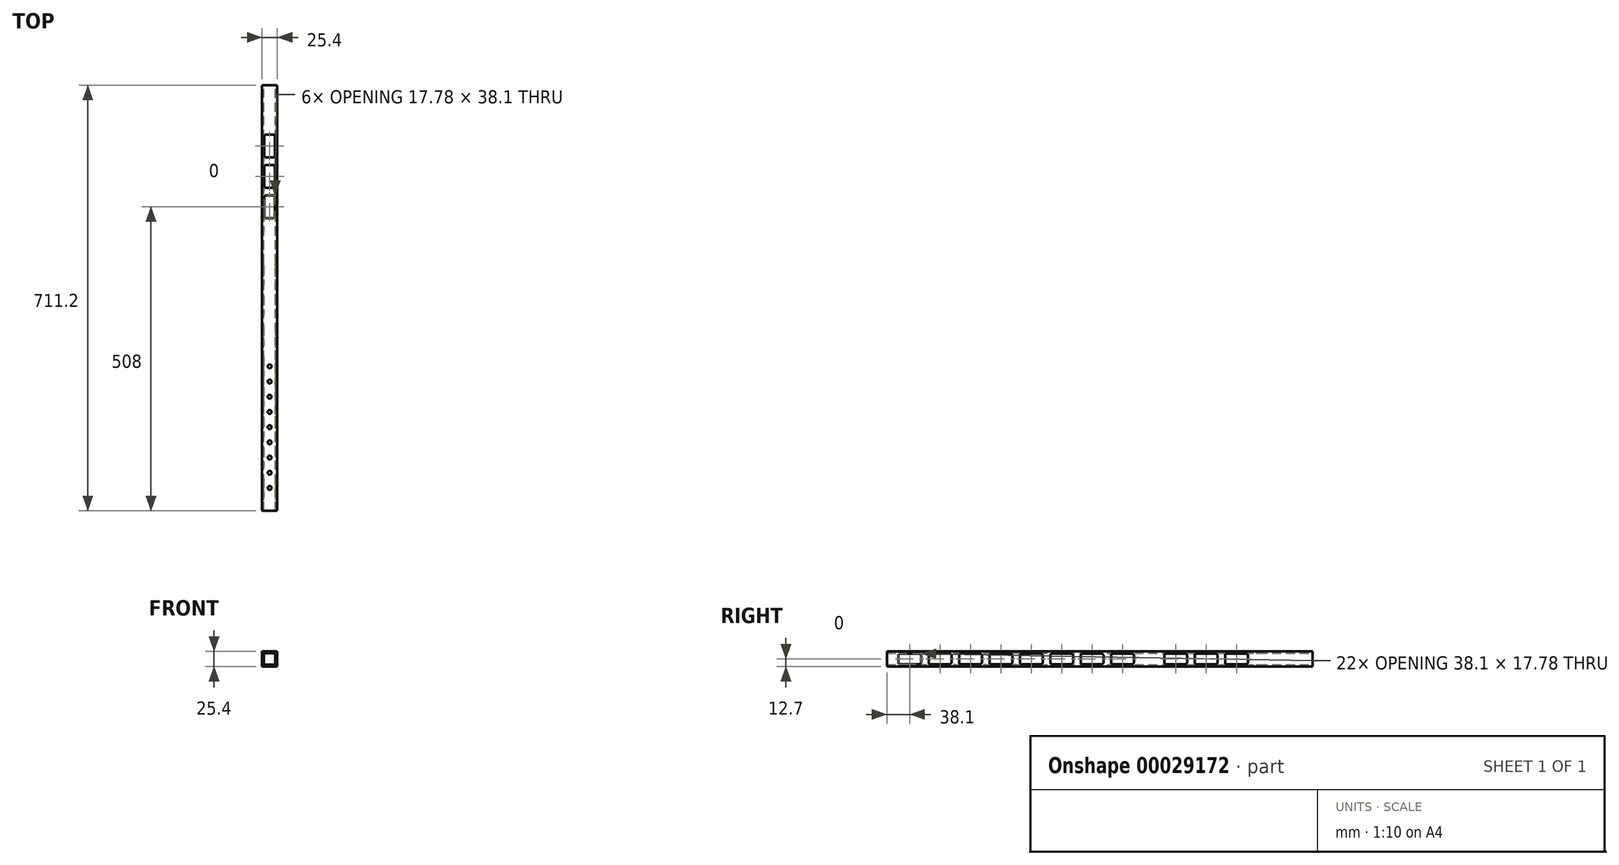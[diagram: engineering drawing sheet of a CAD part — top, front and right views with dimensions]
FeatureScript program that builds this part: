
annotation { "Feature Type Name" : "Feature", "Feature Type Description" : "" }
export const myFeature = defineFeature(function(context is Context, id is Id, definition is map)
    precondition{}
    {
        {
            var Q0;
            Q0=qCreatedBy(makeId("Front.planeOp"),FACE);
            var sketch = newSketch(context, id + "F0", { "sketchPlane" : qUnion([Q0])});
            skLineSegment(sketch, "E0.rect.bottom", {"start": v(12.7, 12.7) * mm, "end": v(-12.7, 12.7) * mm});
            skLineSegment(sketch, "E0.rect.top", {"start": v(12.7, -12.7) * mm, "end": v(-12.7, -12.7) * mm});
            skLineSegment(sketch, "E0.rect.left", {"start": v(12.7, 12.7) * mm, "end": v(12.7, -12.7) * mm});
            skLineSegment(sketch, "E0.rect.right", {"start": v(-12.7, 12.7) * mm, "end": v(-12.7, -12.7) * mm});
            skPoint(sketch, "E0.rect.middle", {"position": v(0, 0) * mm});
            skLineSegment(sketch, "E1.rect.bottom", {"start": v(9.53, 9.53) * mm, "end": v(-9.53, 9.53) * mm});
            skLineSegment(sketch, "E1.rect.top", {"start": v(9.53, -9.53) * mm, "end": v(-9.53, -9.53) * mm});
            skLineSegment(sketch, "E1.rect.left", {"start": v(9.53, 9.53) * mm, "end": v(9.53, -9.53) * mm});
            skLineSegment(sketch, "E1.rect.right", {"start": v(-9.53, 9.53) * mm, "end": v(-9.53, -9.53) * mm});
            skSolve(sketch);
        }
        {
            var Q0;
            Q0=makeQuery(id+"F0.imprint","IMPRINT",FACE,{"disambiguationData":[TD([[makeQuery(id+"F0.imprint","IMPRINT",EDGE,{"derivedFrom":sQuery(id+"F0.wireOp",EDGE,"E0.rect.bottom")}),1.0]])]});
            extrude(context, id + "F1", {"entities" : qUnion([Q0]), "depth" : 279.4 * mm});
        }
        {
            var Q0;
            Q0=makeQuery(id+"F1.opExtrude","CAP_FACE",FACE,{"disambiguationData":[OSD([sQuery(id+"F0.wireOp",EDGE,"E0.rect.bottom"),sQuery(id+"F0.wireOp",EDGE,"E0.rect.top"),sQuery(id+"F0.wireOp",EDGE,"E0.rect.left"),sQuery(id+"F0.wireOp",EDGE,"E0.rect.right"),sQuery(id+"F0.wireOp",EDGE,"E1.rect.bottom"),sQuery(id+"F0.wireOp",EDGE,"E1.rect.top"),sQuery(id+"F0.wireOp",EDGE,"E1.rect.left"),sQuery(id+"F0.wireOp",EDGE,"E1.rect.right")])],"isStart":false});
            extrude(context, id + "F2", {"entities" : qUnion([Q0]), "operationType" : NewBodyOperationType.ADD, "depth" : 431.8 * mm});
        }
        {
            var Q0;
            {var subQ0=sQuery(id+"F0.wireOp",EDGE,"E0.rect.bottom");Q0=makeQuery(id+"F2.boolean.opBoolean","MERGE",FACE,{"derivedFrom":[makeQuery(id+"F1.opExtrude","SWEPT_FACE",FACE,{"disambiguationData":[OSD([subQ0])]}),makeQuery(id+"F2.opExtrude","SWEPT_FACE",FACE,{"disambiguationData":[OSD([subQ0])]})]});}
            var sketch = newSketch(context, id + "F3", { "sketchPlane" : qUnion([Q0])});
            skLineSegment(sketch, "E2", {"start": v(0, -711.2) * mm, "end": v(0, -676.27) * mm});
            skCircle(sketch, "E3", {"center": v(0, -469.9) * mm, "radius": 3.18 * mm});
            skLineSegment(sketch, "E4.trimOffspring", {"start": v(0, -466.73) * mm, "end": v(0, -120.65) * mm});
            skCircle(sketch, "E5", {"center": v(0, -495.3) * mm, "radius": 3.18 * mm});
            skLineSegment(sketch, "E6.trimOffspring", {"start": v(0, -492.13) * mm, "end": v(0, -473.08) * mm});
            skCircle(sketch, "E7", {"center": v(0, -520.7) * mm, "radius": 3.18 * mm});
            skLineSegment(sketch, "E8.trimOffspring", {"start": v(0, -517.52) * mm, "end": v(0, -498.48) * mm});
            skCircle(sketch, "E9", {"center": v(0, -546.1) * mm, "radius": 3.18 * mm});
            skCircle(sketch, "E10", {"center": v(0, -571.5) * mm, "radius": 3.18 * mm});
            skLineSegment(sketch, "E11.trimOffspring", {"start": v(0, -542.92) * mm, "end": v(0, -523.88) * mm});
            skLineSegment(sketch, "E12", {"start": v(0, -549.28) * mm, "end": v(0, -568.32) * mm});
            skCircle(sketch, "E13", {"center": v(0, -596.9) * mm, "radius": 3.18 * mm});
            skLineSegment(sketch, "E14.trimOffspring", {"start": v(0, -593.72) * mm, "end": v(0, -574.68) * mm});
            skCircle(sketch, "E15", {"center": v(0, -622.3) * mm, "radius": 3.18 * mm});
            skLineSegment(sketch, "E16.trimOffspring", {"start": v(0, -619.12) * mm, "end": v(0, -600.08) * mm});
            skCircle(sketch, "E17", {"center": v(0, -647.7) * mm, "radius": 3.18 * mm});
            skLineSegment(sketch, "E18.trimOffspring", {"start": v(0, -644.52) * mm, "end": v(0, -625.48) * mm});
            skCircle(sketch, "E19", {"center": v(0, -673.1) * mm, "radius": 3.18 * mm});
            skLineSegment(sketch, "E20.trimOffspring", {"start": v(0, -669.92) * mm, "end": v(0, -650.88) * mm});
            skLineSegment(sketch, "E21.rect.bottom", {"start": v(-5.71, -82.55) * mm, "end": v(5.72, -82.55) * mm});
            skLineSegment(sketch, "E21.rect.top", {"start": v(-5.71, -120.65) * mm, "end": v(5.72, -120.65) * mm});
            skLineSegment(sketch, "E21.rect.left", {"start": v(-8.89, -85.73) * mm, "end": v(-8.89, -117.48) * mm});
            skLineSegment(sketch, "E21.rect.right", {"start": v(8.9, -85.73) * mm, "end": v(8.9, -117.48) * mm});
            skPoint(sketch, "E21.rect.middle", {"position": v(0, -101.6) * mm});
            skPoint(sketch, "E22.visualSharp", {"position": v(-8.89, -82.55) * mm});
            skArc(sketch, "E22.filletArc", {"start": v(-5.71, -82.55) * mm, "mid": v(-7.96, -83.48) * mm, "end": v(-8.89, -85.73) * mm});
            skPoint(sketch, "E23.visualSharp", {"position": v(8.9, -82.55) * mm});
            skArc(sketch, "E23.filletArc", {"start": v(8.9, -85.73) * mm, "mid": v(7.96, -83.48) * mm, "end": v(5.72, -82.55) * mm});
            skPoint(sketch, "E24.visualSharp", {"position": v(-8.89, -120.65) * mm});
            skArc(sketch, "E24.filletArc", {"start": v(-8.89, -117.48) * mm, "mid": v(-7.96, -119.72) * mm, "end": v(-5.71, -120.65) * mm});
            skPoint(sketch, "E25.visualSharp", {"position": v(8.9, -120.65) * mm});
            skArc(sketch, "E25.filletArc", {"start": v(5.72, -120.65) * mm, "mid": v(7.96, -119.72) * mm, "end": v(8.9, -117.48) * mm});
            skPoint(sketch, "E26", {"position": v(0, -82.55) * mm});
            skLineSegment(sketch, "E27.trimOffspring", {"start": v(0, -82.55) * mm, "end": v(0, 0) * mm});
            skLineSegment(sketch, "E28.0.1.0", {"start": v(-5.71, -171.45) * mm, "end": v(5.72, -171.45) * mm});
            skArc(sketch, "E28.0.1.1", {"start": v(5.72, -171.45) * mm, "mid": v(7.96, -170.52) * mm, "end": v(8.9, -168.28) * mm});
            skLineSegment(sketch, "E28.0.1.2", {"start": v(8.9, -136.53) * mm, "end": v(8.9, -168.28) * mm});
            skArc(sketch, "E28.0.1.3", {"start": v(8.9, -136.53) * mm, "mid": v(7.96, -134.28) * mm, "end": v(5.72, -133.35) * mm});
            skLineSegment(sketch, "E28.0.1.4", {"start": v(-5.71, -133.35) * mm, "end": v(5.72, -133.35) * mm});
            skArc(sketch, "E28.0.1.5", {"start": v(-5.71, -133.35) * mm, "mid": v(-7.96, -134.28) * mm, "end": v(-8.89, -136.53) * mm});
            skLineSegment(sketch, "E28.0.1.6", {"start": v(-8.89, -136.53) * mm, "end": v(-8.89, -168.28) * mm});
            skArc(sketch, "E28.0.1.7", {"start": v(-8.89, -168.28) * mm, "mid": v(-7.96, -170.52) * mm, "end": v(-5.71, -171.45) * mm});
            skLineSegment(sketch, "E28.0.2.0", {"start": v(-5.71, -222.25) * mm, "end": v(5.72, -222.25) * mm});
            skArc(sketch, "E28.0.2.1", {"start": v(5.72, -222.25) * mm, "mid": v(7.96, -221.32) * mm, "end": v(8.9, -219.08) * mm});
            skLineSegment(sketch, "E28.0.2.2", {"start": v(8.9, -187.33) * mm, "end": v(8.9, -219.08) * mm});
            skArc(sketch, "E28.0.2.3", {"start": v(8.9, -187.33) * mm, "mid": v(7.96, -185.08) * mm, "end": v(5.72, -184.15) * mm});
            skLineSegment(sketch, "E28.0.2.4", {"start": v(-5.71, -184.15) * mm, "end": v(5.72, -184.15) * mm});
            skArc(sketch, "E28.0.2.5", {"start": v(-5.71, -184.15) * mm, "mid": v(-7.96, -185.08) * mm, "end": v(-8.89, -187.33) * mm});
            skLineSegment(sketch, "E28.0.2.6", {"start": v(-8.89, -187.33) * mm, "end": v(-8.89, -219.08) * mm});
            skArc(sketch, "E28.0.2.7", {"start": v(-8.89, -219.08) * mm, "mid": v(-7.96, -221.32) * mm, "end": v(-5.71, -222.25) * mm});
            skLineSegment(sketch, "E28.direction1", {"start": v(-5.71, -120.65) * mm, "end": v(44.46, -120.65) * mm, "construction": true});
            skLineSegment(sketch, "E28.direction2", {"start": v(-5.71, -120.65) * mm, "end": v(-5.71, -171.45) * mm, "construction": true});
            skSolve(sketch);
        }
        {
            var Q0;
            {var subQ0=sQuery(id+"F3.wireOp",EDGE,"E3");var subQ2=makeQuery(id+"F3.imprint","INTERSECT",VERTEX,{"derivedFrom":[sQuery(id+"F3.wireOp",EDGE,"E2"),subQ0]});Q0=makeQuery(id+"F3.imprint","IMPRINT",FACE,{"disambiguationData":[TD([[makeQuery(id+"F3.imprint","IMPRINT",EDGE,{"disambiguationData":[TD([[subQ2,1.0]])],"derivedFrom":subQ0}),1.0]])]});}
            extrude(context, id + "F4", {"entities" : qUnion([Q0]), "operationType" : NewBodyOperationType.REMOVE, "oppositeDirection" : true, "depth" : 25.4 * mm});
        }
        {
            var Q0;
            Q0 = qSketchRegion(id + "F3", true);
            extrude(context, id + "F5", {"entities" : qUnion([Q0]), "operationType" : NewBodyOperationType.REMOVE, "oppositeDirection" : true, "depth" : 25.4 * mm});
        }
        {
            var Q0;
            {var subQ0=sQuery(id+"F0.wireOp",EDGE,"E0.rect.left");Q0=makeQuery(id+"F2.boolean.opBoolean","MERGE",FACE,{"derivedFrom":[makeQuery(id+"F1.opExtrude","SWEPT_FACE",FACE,{"disambiguationData":[OSD([subQ0])]}),makeQuery(id+"F2.opExtrude","SWEPT_FACE",FACE,{"disambiguationData":[OSD([subQ0])]})]});}
            var sketch = newSketch(context, id + "F6", { "sketchPlane" : qUnion([Q0])});
            skLineSegment(sketch, "E29", {"start": v(0, 0) * mm, "end": v(-57.15, 0) * mm});
            skLineSegment(sketch, "E30.rect.bottom", {"start": v(-657.23, -8.9) * mm, "end": v(-688.98, -8.9) * mm});
            skLineSegment(sketch, "E30.rect.top", {"start": v(-657.23, 8.9) * mm, "end": v(-688.98, 8.9) * mm});
            skLineSegment(sketch, "E30.rect.left", {"start": v(-654.05, -5.72) * mm, "end": v(-654.05, 5.72) * mm});
            skLineSegment(sketch, "E30.rect.right", {"start": v(-692.15, -5.72) * mm, "end": v(-692.15, 5.72) * mm});
            skPoint(sketch, "E30.rect.middle", {"position": v(-673.1, 0) * mm});
            skPoint(sketch, "E31.visualSharp", {"position": v(-654.05, 8.89) * mm});
            skArc(sketch, "E31.filletArc", {"start": v(-654.05, 5.72) * mm, "mid": v(-654.98, 7.96) * mm, "end": v(-657.23, 8.9) * mm});
            skPoint(sketch, "E32.visualSharp", {"position": v(-654.05, -8.9) * mm});
            skArc(sketch, "E32.filletArc", {"start": v(-657.23, -8.9) * mm, "mid": v(-654.98, -7.96) * mm, "end": v(-654.05, -5.72) * mm});
            skPoint(sketch, "E33.visualSharp", {"position": v(-692.15, -8.9) * mm});
            skArc(sketch, "E33.filletArc", {"start": v(-692.15, -5.72) * mm, "mid": v(-691.22, -7.96) * mm, "end": v(-688.98, -8.9) * mm});
            skPoint(sketch, "E34.visualSharp", {"position": v(-692.15, 8.89) * mm});
            skArc(sketch, "E34.filletArc", {"start": v(-688.98, 8.9) * mm, "mid": v(-691.22, 7.96) * mm, "end": v(-692.15, 5.72) * mm});
            skLineSegment(sketch, "E35.trimOffspring", {"start": v(-692.15, 0) * mm, "end": v(-711.2, 0) * mm});
            skLineSegment(sketch, "E36.1.0.0", {"start": v(-603.25, -5.72) * mm, "end": v(-603.25, 5.72) * mm});
            skArc(sketch, "E36.1.0.1", {"start": v(-603.25, 5.72) * mm, "mid": v(-604.18, 7.96) * mm, "end": v(-606.43, 8.9) * mm});
            skLineSegment(sketch, "E36.1.0.2", {"start": v(-606.43, -8.9) * mm, "end": v(-638.18, -8.9) * mm});
            skArc(sketch, "E36.1.0.3", {"start": v(-606.43, -8.9) * mm, "mid": v(-604.18, -7.96) * mm, "end": v(-603.25, -5.72) * mm});
            skLineSegment(sketch, "E36.1.0.4", {"start": v(-606.43, 8.9) * mm, "end": v(-638.18, 8.9) * mm});
            skArc(sketch, "E36.1.0.5", {"start": v(-638.18, 8.9) * mm, "mid": v(-640.42, 7.96) * mm, "end": v(-641.35, 5.72) * mm});
            skLineSegment(sketch, "E36.1.0.6", {"start": v(-641.35, -5.72) * mm, "end": v(-641.35, 5.72) * mm});
            skArc(sketch, "E36.1.0.7", {"start": v(-641.35, -5.72) * mm, "mid": v(-640.42, -7.96) * mm, "end": v(-638.18, -8.9) * mm});
            skLineSegment(sketch, "E36.2.0.0", {"start": v(-552.45, -5.72) * mm, "end": v(-552.45, 5.72) * mm});
            skArc(sketch, "E36.2.0.1", {"start": v(-552.45, 5.72) * mm, "mid": v(-553.38, 7.96) * mm, "end": v(-555.63, 8.9) * mm});
            skLineSegment(sketch, "E36.2.0.2", {"start": v(-555.63, -8.9) * mm, "end": v(-587.38, -8.9) * mm});
            skArc(sketch, "E36.2.0.3", {"start": v(-555.63, -8.9) * mm, "mid": v(-553.38, -7.96) * mm, "end": v(-552.45, -5.72) * mm});
            skLineSegment(sketch, "E36.2.0.4", {"start": v(-555.63, 8.9) * mm, "end": v(-587.38, 8.9) * mm});
            skArc(sketch, "E36.2.0.5", {"start": v(-587.38, 8.9) * mm, "mid": v(-589.62, 7.96) * mm, "end": v(-590.55, 5.72) * mm});
            skLineSegment(sketch, "E36.2.0.6", {"start": v(-590.55, -5.72) * mm, "end": v(-590.55, 5.72) * mm});
            skArc(sketch, "E36.2.0.7", {"start": v(-590.55, -5.72) * mm, "mid": v(-589.62, -7.96) * mm, "end": v(-587.38, -8.9) * mm});
            skLineSegment(sketch, "E36.3.0.0", {"start": v(-501.65, -5.72) * mm, "end": v(-501.65, 5.72) * mm});
            skArc(sketch, "E36.3.0.1", {"start": v(-501.65, 5.72) * mm, "mid": v(-502.58, 7.96) * mm, "end": v(-504.83, 8.9) * mm});
            skLineSegment(sketch, "E36.3.0.2", {"start": v(-504.83, -8.9) * mm, "end": v(-536.58, -8.9) * mm});
            skArc(sketch, "E36.3.0.3", {"start": v(-504.83, -8.9) * mm, "mid": v(-502.58, -7.96) * mm, "end": v(-501.65, -5.72) * mm});
            skLineSegment(sketch, "E36.3.0.4", {"start": v(-504.83, 8.9) * mm, "end": v(-536.58, 8.9) * mm});
            skArc(sketch, "E36.3.0.5", {"start": v(-536.58, 8.9) * mm, "mid": v(-538.82, 7.96) * mm, "end": v(-539.75, 5.72) * mm});
            skLineSegment(sketch, "E36.3.0.6", {"start": v(-539.75, -5.72) * mm, "end": v(-539.75, 5.72) * mm});
            skArc(sketch, "E36.3.0.7", {"start": v(-539.75, -5.72) * mm, "mid": v(-538.82, -7.96) * mm, "end": v(-536.58, -8.9) * mm});
            skLineSegment(sketch, "E36.4.0.0", {"start": v(-450.85, -5.72) * mm, "end": v(-450.85, 5.72) * mm});
            skArc(sketch, "E36.4.0.1", {"start": v(-450.85, 5.72) * mm, "mid": v(-451.78, 7.96) * mm, "end": v(-454.03, 8.9) * mm});
            skLineSegment(sketch, "E36.4.0.2", {"start": v(-454.03, -8.9) * mm, "end": v(-485.78, -8.9) * mm});
            skArc(sketch, "E36.4.0.3", {"start": v(-454.03, -8.9) * mm, "mid": v(-451.78, -7.96) * mm, "end": v(-450.85, -5.72) * mm});
            skLineSegment(sketch, "E36.4.0.4", {"start": v(-454.03, 8.9) * mm, "end": v(-485.78, 8.9) * mm});
            skArc(sketch, "E36.4.0.5", {"start": v(-485.78, 8.9) * mm, "mid": v(-488.02, 7.96) * mm, "end": v(-488.95, 5.72) * mm});
            skLineSegment(sketch, "E36.4.0.6", {"start": v(-488.95, -5.72) * mm, "end": v(-488.95, 5.72) * mm});
            skArc(sketch, "E36.4.0.7", {"start": v(-488.95, -5.72) * mm, "mid": v(-488.02, -7.96) * mm, "end": v(-485.78, -8.9) * mm});
            skLineSegment(sketch, "E36.5.0.0", {"start": v(-400.05, -5.72) * mm, "end": v(-400.05, 5.72) * mm});
            skArc(sketch, "E36.5.0.1", {"start": v(-400.05, 5.72) * mm, "mid": v(-400.98, 7.96) * mm, "end": v(-403.23, 8.9) * mm});
            skLineSegment(sketch, "E36.5.0.2", {"start": v(-403.23, -8.9) * mm, "end": v(-434.98, -8.9) * mm});
            skArc(sketch, "E36.5.0.3", {"start": v(-403.23, -8.9) * mm, "mid": v(-400.98, -7.96) * mm, "end": v(-400.05, -5.72) * mm});
            skLineSegment(sketch, "E36.5.0.4", {"start": v(-403.23, 8.9) * mm, "end": v(-434.98, 8.9) * mm});
            skArc(sketch, "E36.5.0.5", {"start": v(-434.98, 8.9) * mm, "mid": v(-437.22, 7.96) * mm, "end": v(-438.15, 5.72) * mm});
            skLineSegment(sketch, "E36.5.0.6", {"start": v(-438.15, -5.72) * mm, "end": v(-438.15, 5.72) * mm});
            skArc(sketch, "E36.5.0.7", {"start": v(-438.15, -5.72) * mm, "mid": v(-437.22, -7.96) * mm, "end": v(-434.98, -8.9) * mm});
            skLineSegment(sketch, "E36.6.0.0", {"start": v(-349.25, -5.72) * mm, "end": v(-349.25, 5.72) * mm});
            skArc(sketch, "E36.6.0.1", {"start": v(-349.25, 5.72) * mm, "mid": v(-350.18, 7.96) * mm, "end": v(-352.43, 8.9) * mm});
            skLineSegment(sketch, "E36.6.0.2", {"start": v(-352.43, -8.9) * mm, "end": v(-384.18, -8.9) * mm});
            skArc(sketch, "E36.6.0.3", {"start": v(-352.43, -8.9) * mm, "mid": v(-350.18, -7.96) * mm, "end": v(-349.25, -5.72) * mm});
            skLineSegment(sketch, "E36.6.0.4", {"start": v(-352.43, 8.9) * mm, "end": v(-384.18, 8.9) * mm});
            skArc(sketch, "E36.6.0.5", {"start": v(-384.18, 8.9) * mm, "mid": v(-386.42, 7.96) * mm, "end": v(-387.35, 5.72) * mm});
            skLineSegment(sketch, "E36.6.0.6", {"start": v(-387.35, -5.72) * mm, "end": v(-387.35, 5.72) * mm});
            skArc(sketch, "E36.6.0.7", {"start": v(-387.35, -5.72) * mm, "mid": v(-386.42, -7.96) * mm, "end": v(-384.18, -8.9) * mm});
            skLineSegment(sketch, "E36.7.0.0", {"start": v(-298.45, -5.72) * mm, "end": v(-298.45, 5.72) * mm});
            skArc(sketch, "E36.7.0.1", {"start": v(-298.45, 5.72) * mm, "mid": v(-299.38, 7.96) * mm, "end": v(-301.63, 8.9) * mm});
            skLineSegment(sketch, "E36.7.0.2", {"start": v(-301.63, -8.9) * mm, "end": v(-333.38, -8.9) * mm});
            skArc(sketch, "E36.7.0.3", {"start": v(-301.63, -8.9) * mm, "mid": v(-299.38, -7.96) * mm, "end": v(-298.45, -5.72) * mm});
            skLineSegment(sketch, "E36.7.0.4", {"start": v(-301.63, 8.9) * mm, "end": v(-333.38, 8.9) * mm});
            skArc(sketch, "E36.7.0.5", {"start": v(-333.38, 8.9) * mm, "mid": v(-335.62, 7.96) * mm, "end": v(-336.55, 5.72) * mm});
            skLineSegment(sketch, "E36.7.0.6", {"start": v(-336.55, -5.72) * mm, "end": v(-336.55, 5.72) * mm});
            skArc(sketch, "E36.7.0.7", {"start": v(-336.55, -5.72) * mm, "mid": v(-335.62, -7.96) * mm, "end": v(-333.38, -8.9) * mm});
            skLineSegment(sketch, "E36.direction1", {"start": v(-654.05, -5.72) * mm, "end": v(-603.25, -5.72) * mm, "construction": true});
            skLineSegment(sketch, "E37.1.0.0", {"start": v(-209.55, -5.72) * mm, "end": v(-209.55, 5.72) * mm});
            skArc(sketch, "E37.1.0.1", {"start": v(-209.55, 5.72) * mm, "mid": v(-210.48, 7.96) * mm, "end": v(-212.73, 8.9) * mm});
            skLineSegment(sketch, "E37.1.0.2", {"start": v(-212.73, 8.9) * mm, "end": v(-244.48, 8.9) * mm});
            skArc(sketch, "E37.1.0.3", {"start": v(-244.48, 8.9) * mm, "mid": v(-246.72, 7.96) * mm, "end": v(-247.65, 5.72) * mm});
            skLineSegment(sketch, "E37.1.0.4", {"start": v(-247.65, -5.72) * mm, "end": v(-247.65, 5.72) * mm});
            skLineSegment(sketch, "E37.1.0.5", {"start": v(-212.73, -8.9) * mm, "end": v(-244.48, -8.9) * mm});
            skArc(sketch, "E37.1.0.6", {"start": v(-247.65, -5.72) * mm, "mid": v(-246.72, -7.96) * mm, "end": v(-244.48, -8.9) * mm});
            skArc(sketch, "E37.1.0.7", {"start": v(-212.73, -8.9) * mm, "mid": v(-210.48, -7.96) * mm, "end": v(-209.55, -5.72) * mm});
            skLineSegment(sketch, "E37.direction1", {"start": v(-298.45, -5.72) * mm, "end": v(-209.55, -5.72) * mm, "construction": true});
            skLineSegment(sketch, "E38.1.0.0", {"start": v(-158.75, -5.72) * mm, "end": v(-158.75, 5.72) * mm});
            skArc(sketch, "E38.1.0.1", {"start": v(-158.75, 5.72) * mm, "mid": v(-159.68, 7.96) * mm, "end": v(-161.93, 8.9) * mm});
            skLineSegment(sketch, "E38.1.0.2", {"start": v(-161.93, 8.9) * mm, "end": v(-193.68, 8.9) * mm});
            skArc(sketch, "E38.1.0.3", {"start": v(-193.68, 8.9) * mm, "mid": v(-195.92, 7.96) * mm, "end": v(-196.85, 5.72) * mm});
            skLineSegment(sketch, "E38.1.0.4", {"start": v(-196.85, -5.72) * mm, "end": v(-196.85, 5.72) * mm});
            skArc(sketch, "E38.1.0.5", {"start": v(-196.85, -5.72) * mm, "mid": v(-195.92, -7.96) * mm, "end": v(-193.68, -8.9) * mm});
            skLineSegment(sketch, "E38.1.0.6", {"start": v(-161.93, -8.9) * mm, "end": v(-193.68, -8.9) * mm});
            skArc(sketch, "E38.1.0.7", {"start": v(-161.93, -8.9) * mm, "mid": v(-159.68, -7.96) * mm, "end": v(-158.75, -5.72) * mm});
            skLineSegment(sketch, "E38.2.0.0", {"start": v(-107.95, -5.72) * mm, "end": v(-107.95, 5.72) * mm});
            skArc(sketch, "E38.2.0.1", {"start": v(-107.95, 5.72) * mm, "mid": v(-108.88, 7.96) * mm, "end": v(-111.13, 8.9) * mm});
            skLineSegment(sketch, "E38.2.0.2", {"start": v(-111.13, 8.9) * mm, "end": v(-142.88, 8.9) * mm});
            skArc(sketch, "E38.2.0.3", {"start": v(-142.88, 8.9) * mm, "mid": v(-145.12, 7.96) * mm, "end": v(-146.05, 5.72) * mm});
            skLineSegment(sketch, "E38.2.0.4", {"start": v(-146.05, -5.72) * mm, "end": v(-146.05, 5.72) * mm});
            skArc(sketch, "E38.2.0.5", {"start": v(-146.05, -5.72) * mm, "mid": v(-145.12, -7.96) * mm, "end": v(-142.88, -8.9) * mm});
            skLineSegment(sketch, "E38.2.0.6", {"start": v(-111.13, -8.9) * mm, "end": v(-142.88, -8.9) * mm});
            skArc(sketch, "E38.2.0.7", {"start": v(-111.13, -8.9) * mm, "mid": v(-108.88, -7.96) * mm, "end": v(-107.95, -5.72) * mm});
            skLineSegment(sketch, "E38.direction1", {"start": v(-209.55, -5.72) * mm, "end": v(-158.75, -5.72) * mm, "construction": true});
            skLineSegment(sketch, "E39.trimOffspring", {"start": v(-641.35, 0) * mm, "end": v(-654.05, 0) * mm});
            skLineSegment(sketch, "E40.trimOffspring", {"start": v(-590.55, 0) * mm, "end": v(-603.25, 0) * mm});
            skLineSegment(sketch, "E41.trimOffspring", {"start": v(-539.75, 0) * mm, "end": v(-552.45, 0) * mm});
            skLineSegment(sketch, "E42.trimOffspring", {"start": v(-488.95, 0) * mm, "end": v(-501.65, 0) * mm});
            skLineSegment(sketch, "E43.trimOffspring", {"start": v(-438.15, 0) * mm, "end": v(-450.85, 0) * mm});
            skLineSegment(sketch, "E44.trimOffspring", {"start": v(-387.35, 0) * mm, "end": v(-400.05, 0) * mm});
            skLineSegment(sketch, "E45.trimOffspring", {"start": v(-336.55, 0) * mm, "end": v(-349.25, 0) * mm});
            skLineSegment(sketch, "E46.trimOffspring", {"start": v(-247.65, 0) * mm, "end": v(-298.45, 0) * mm});
            skLineSegment(sketch, "E47.trimOffspring", {"start": v(-196.85, 0) * mm, "end": v(-209.55, 0) * mm});
            skLineSegment(sketch, "E48.trimOffspring", {"start": v(-146.05, 0) * mm, "end": v(-158.75, 0) * mm});
            skLineSegment(sketch, "E49.trimOffspring", {"start": v(-95.25, 0) * mm, "end": v(-107.95, 0) * mm});
            skLineSegment(sketch, "E50", {"start": v(-57.15, 0) * mm, "end": v(-95.25, 0) * mm});
            skLineSegment(sketch, "E51", {"start": v(-273.05, 0) * mm, "end": v(-273.05, 12.7) * mm});
            skLineSegment(sketch, "E52", {"start": v(-273.05, 0) * mm, "end": v(-273.05, -12.7) * mm});
            skSolve(sketch);
        }
        {
            var Q0;
            Q0 = qSketchRegion(id + "F6", true);
            extrude(context, id + "F7", {"entities" : qUnion([Q0]), "operationType" : NewBodyOperationType.REMOVE, "oppositeDirection" : true, "depth" : 25.4 * mm});
        }
    });
